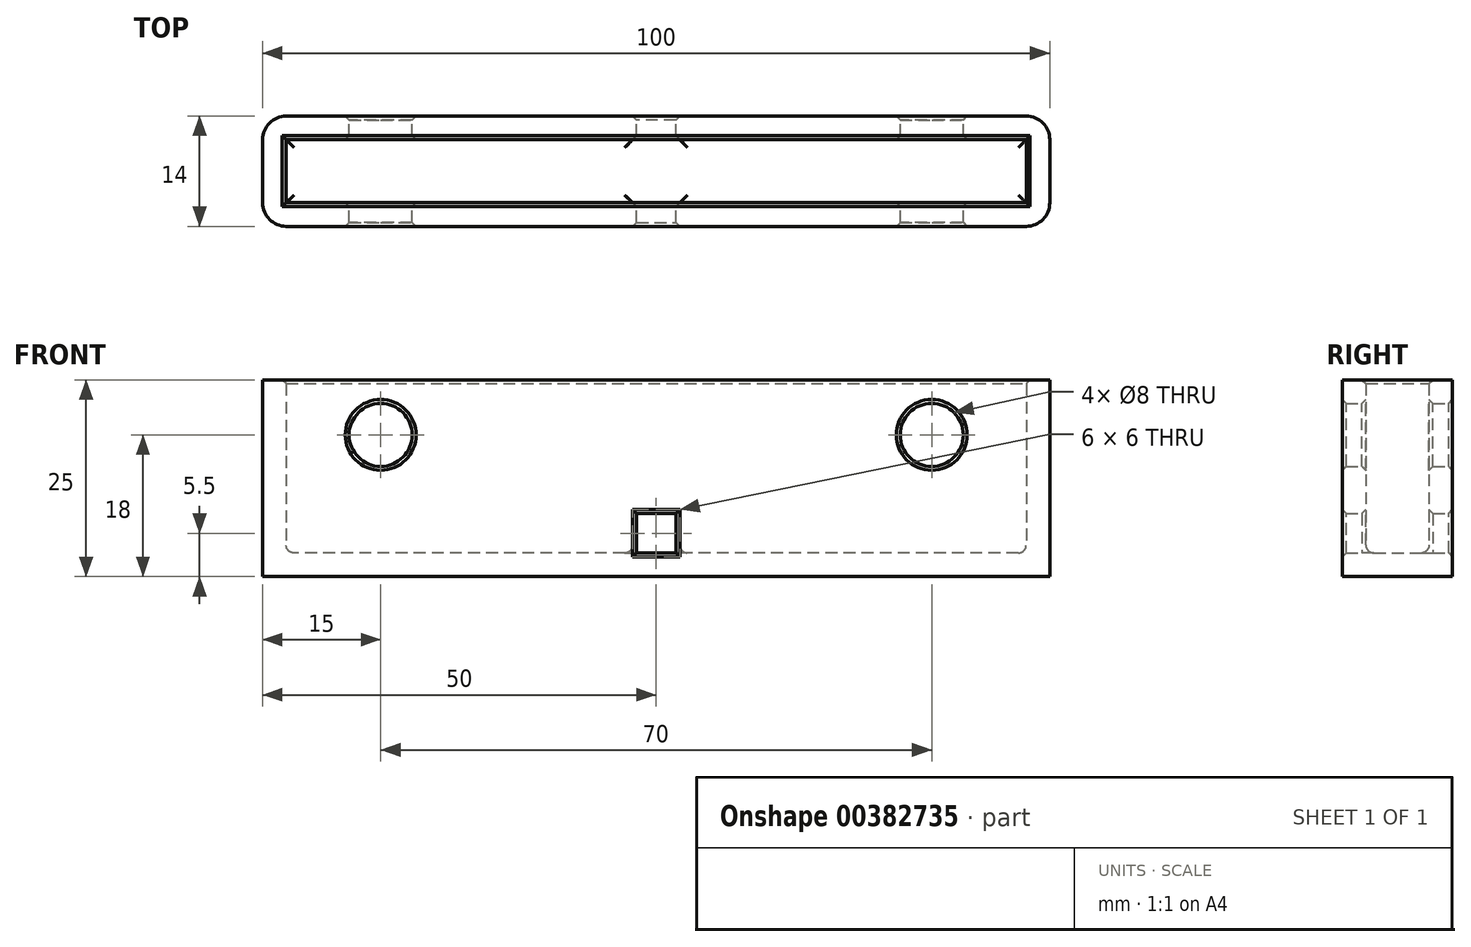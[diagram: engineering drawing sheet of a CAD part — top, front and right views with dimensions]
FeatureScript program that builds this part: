
annotation { "Feature Type Name" : "Feature", "Feature Type Description" : "" }
export const myFeature = defineFeature(function(context is Context, id is Id, definition is map)
    precondition{}
    {
        {
            var Q0;
            Q0=qCreatedBy(makeId("Top.planeOp"),FACE);
            var sketch = newSketch(context, id + "F0", { "sketchPlane" : qUnion([Q0])});
            skLineSegment(sketch, "E0.bottom", {"start": v(50, -7) * mm, "end": v(-50, -7) * mm});
            skLineSegment(sketch, "E0.top", {"start": v(50, 7) * mm, "end": v(-50, 7) * mm});
            skLineSegment(sketch, "E0.left", {"start": v(50, -7) * mm, "end": v(50, 7) * mm});
            skLineSegment(sketch, "E0.right", {"start": v(-50, -7) * mm, "end": v(-50, 7) * mm});
            skPoint(sketch, "E0.middle", {"position": v(0, 0) * mm});
            skSolve(sketch);
        }
        {
            var Q0;
            Q0=makeQuery(id+"F0.imprint","IMPRINT",FACE,{"disambiguationData":[TD([[makeQuery(id+"F0.imprint","IMPRINT",EDGE,{"derivedFrom":sQuery(id+"F0.wireOp",EDGE,"E0.bottom")}),-1.0]])]});
            extrude(context, id + "F1", {"entities" : qUnion([Q0]), "depth" : 25 * mm});
        }
        {
            var Q0;
            Q0=makeQuery(id+"F1.opExtrude","CAP_FACE",FACE,{"disambiguationData":[OSD([sQuery(id+"F0.wireOp",EDGE,"E0.bottom"),sQuery(id+"F0.wireOp",EDGE,"E0.top"),sQuery(id+"F0.wireOp",EDGE,"E0.left"),sQuery(id+"F0.wireOp",EDGE,"E0.right")])],"isStart":false});
            shell(context, id + "F2", {"entities" : qUnion([Q0]), "thickness" : 3 * mm});
        }
        {
            var Q0;
            Q0=qCreatedBy(makeId("Front.planeOp"),FACE);
            var sketch = newSketch(context, id + "F3", { "sketchPlane" : qUnion([Q0])});
            skCircle(sketch, "E1", {"center": v(-35, 18) * mm, "radius": 4 * mm});
            skCircle(sketch, "E2", {"center": v(35, 18) * mm, "radius": 4 * mm});
            skLineSegment(sketch, "E3.bottom", {"start": v(2.5, 8) * mm, "end": v(-2.5, 8) * mm});
            skLineSegment(sketch, "E3.top", {"start": v(2.5, 3) * mm, "end": v(-2.5, 3) * mm});
            skLineSegment(sketch, "E3.left", {"start": v(2.5, 8) * mm, "end": v(2.5, 3) * mm});
            skLineSegment(sketch, "E3.right", {"start": v(-2.5, 8) * mm, "end": v(-2.5, 3) * mm});
            skPoint(sketch, "E3.middle", {"position": v(0, 5.5) * mm});
            skSolve(sketch);
        }
        {
            var Q0;
            Q0 = qSketchRegion(id + "F3", true);
            extrude(context, id + "F4", {"entities" : qUnion([Q0]), "operationType" : NewBodyOperationType.REMOVE, "endBound" : BoundingType.THROUGH_ALL, "depth" : 25 * mm, "hasSecondDirection" : true, "secondDirectionBound" : BoundingType.THROUGH_ALL, "secondDirectionOppositeDirection" : true, "secondDirectionDepth" : 25 * mm});
        }
        {
            var Q0;
            Q0=makeQuery(id+"F1.opExtrude","SWEPT_EDGE",EDGE,{"disambiguationData":[OSD([sQuery(id+"F0.wireOp",EDGE,"E0.bottom"),sQuery(id+"F0.wireOp",EDGE,"E0.right")])]});
            var Q1;
            Q1=makeQuery(id+"F1.opExtrude","SWEPT_EDGE",EDGE,{"disambiguationData":[OSD([sQuery(id+"F0.wireOp",EDGE,"E0.bottom"),sQuery(id+"F0.wireOp",EDGE,"E0.left")])]});
            var Q2;
            Q2=makeQuery(id+"F1.opExtrude","SWEPT_EDGE",EDGE,{"disambiguationData":[OSD([sQuery(id+"F0.wireOp",EDGE,"E0.top"),sQuery(id+"F0.wireOp",EDGE,"E0.left")])]});
            var Q3;
            Q3=makeQuery(id+"F1.opExtrude","SWEPT_EDGE",EDGE,{"disambiguationData":[OSD([sQuery(id+"F0.wireOp",EDGE,"E0.top"),sQuery(id+"F0.wireOp",EDGE,"E0.right")])]});
            fillet(context, id + "F5", {"entities" : qUnion([Q0, Q1, Q2, Q3]), "radius" : 3 * mm, "tangentPropagation" : true, "allowEdgeOverflow" : false});
        }
        {
            var Q0;
            {var subQ0=sQuery(id+"F0.wireOp",EDGE,"E0.top");Q0=makeQuery(id+"F2.opShell","OFFSET_EDGE",EDGE,{"disambiguationData":[OSD([subQ0]),TDD([makeQuery(id+"F1.opExtrude","CAP_EDGE",EDGE,{"disambiguationData":[OSD([subQ0])],"isStart":false})])]});}
            var Q1;
            {var subQ0=sQuery(id+"F0.wireOp",EDGE,"E0.bottom");Q1=makeQuery(id+"F2.opShell","OFFSET_EDGE",EDGE,{"disambiguationData":[OSD([subQ0]),TDD([makeQuery(id+"F1.opExtrude","CAP_EDGE",EDGE,{"disambiguationData":[OSD([subQ0])],"isStart":false})])]});}
            var Q2;
            {var subQ0=sQuery(id+"F0.wireOp",EDGE,"E0.right");Q2=makeQuery(id+"F2.opShell","OFFSET_EDGE",EDGE,{"disambiguationData":[OSD([subQ0]),TDD([makeQuery(id+"F1.opExtrude","CAP_EDGE",EDGE,{"disambiguationData":[OSD([subQ0])],"isStart":false})])]});}
            var Q3;
            {var subQ0=sQuery(id+"F0.wireOp",EDGE,"E0.left");Q3=makeQuery(id+"F2.opShell","OFFSET_EDGE",EDGE,{"disambiguationData":[OSD([subQ0]),TDD([makeQuery(id+"F1.opExtrude","CAP_EDGE",EDGE,{"disambiguationData":[OSD([subQ0])],"isStart":false})])]});}
            var Q4;
            {var subQ0=sQuery(id+"F0.wireOp",EDGE,"E0.top");Q4=makeQuery(id+"F4.boolean.opBoolean","COPY",FACE,{"disambiguationData":[TD([makeQuery(id+"F1.opExtrude","SWEPT_FACE",FACE,{"disambiguationData":[OSD([subQ0])]})])],"derivedFrom":makeQuery(id+"F4.opExtrude","SWEPT_FACE",FACE,{"disambiguationData":[OSD([sQuery(id+"F3.wireOp",EDGE,"E2")])]})});}
            var Q5;
            {var subQ0=sQuery(id+"F0.wireOp",EDGE,"E0.bottom");Q5=makeQuery(id+"F4.boolean.opBoolean","COPY",FACE,{"disambiguationData":[TD([makeQuery(id+"F1.opExtrude","SWEPT_FACE",FACE,{"disambiguationData":[OSD([subQ0])]})])],"derivedFrom":makeQuery(id+"F4.opExtrude","SWEPT_FACE",FACE,{"disambiguationData":[OSD([sQuery(id+"F3.wireOp",EDGE,"E2")])]})});}
            var Q6;
            {var subQ0=sQuery(id+"F0.wireOp",EDGE,"E0.top");Q6=makeQuery(id+"F4.boolean.opBoolean","COPY",FACE,{"disambiguationData":[TD([makeQuery(id+"F1.opExtrude","SWEPT_FACE",FACE,{"disambiguationData":[OSD([subQ0])]})])],"derivedFrom":makeQuery(id+"F4.opExtrude","SWEPT_FACE",FACE,{"disambiguationData":[OSD([sQuery(id+"F3.wireOp",EDGE,"E1")])]})});}
            var Q7;
            {var subQ0=sQuery(id+"F0.wireOp",EDGE,"E0.bottom");Q7=makeQuery(id+"F4.boolean.opBoolean","COPY",FACE,{"disambiguationData":[TD([makeQuery(id+"F1.opExtrude","SWEPT_FACE",FACE,{"disambiguationData":[OSD([subQ0])]})])],"derivedFrom":makeQuery(id+"F4.opExtrude","SWEPT_FACE",FACE,{"disambiguationData":[OSD([sQuery(id+"F3.wireOp",EDGE,"E1")])]})});}
            var Q8;
            Q8=makeQuery(id+"F4.boolean.opBoolean","INTERSECT",EDGE,{"derivedFrom":[makeQuery(id+"F2.opShell","OFFSET_FACE",FACE,{"disambiguationData":[OSD([sQuery(id+"F0.wireOp",EDGE,"E0.bottom")])]}),makeQuery(id+"F4.opExtrude","SWEPT_FACE",FACE,{"disambiguationData":[OSD([sQuery(id+"F3.wireOp",EDGE,"E3.right")])]})]});
            var Q9;
            Q9=makeQuery(id+"F4.boolean.opBoolean","INTERSECT",EDGE,{"derivedFrom":[makeQuery(id+"F2.opShell","OFFSET_FACE",FACE,{"disambiguationData":[OSD([sQuery(id+"F0.wireOp",EDGE,"E0.bottom")])]}),makeQuery(id+"F4.opExtrude","SWEPT_FACE",FACE,{"disambiguationData":[OSD([sQuery(id+"F3.wireOp",EDGE,"E3.bottom")])]})]});
            var Q10;
            Q10=makeQuery(id+"F4.boolean.opBoolean","INTERSECT",EDGE,{"derivedFrom":[makeQuery(id+"F2.opShell","OFFSET_FACE",FACE,{"disambiguationData":[OSD([sQuery(id+"F0.wireOp",EDGE,"E0.bottom")])]}),makeQuery(id+"F4.opExtrude","SWEPT_FACE",FACE,{"disambiguationData":[OSD([sQuery(id+"F3.wireOp",EDGE,"E3.left")])]})]});
            var Q11;
            Q11=makeQuery(id+"F4.boolean.opBoolean","INTERSECT",EDGE,{"derivedFrom":[makeQuery(id+"F2.opShell","OFFSET_FACE",FACE,{"disambiguationData":[OSD([sQuery(id+"F0.wireOp",EDGE,"E0.top")])]}),makeQuery(id+"F4.opExtrude","SWEPT_FACE",FACE,{"disambiguationData":[OSD([sQuery(id+"F3.wireOp",EDGE,"E3.right")])]})]});
            var Q12;
            Q12=makeQuery(id+"F4.boolean.opBoolean","INTERSECT",EDGE,{"derivedFrom":[makeQuery(id+"F2.opShell","OFFSET_FACE",FACE,{"disambiguationData":[OSD([sQuery(id+"F0.wireOp",EDGE,"E0.top")])]}),makeQuery(id+"F4.opExtrude","SWEPT_FACE",FACE,{"disambiguationData":[OSD([sQuery(id+"F3.wireOp",EDGE,"E3.bottom")])]})]});
            var Q13;
            Q13=makeQuery(id+"F4.boolean.opBoolean","INTERSECT",EDGE,{"derivedFrom":[makeQuery(id+"F2.opShell","OFFSET_FACE",FACE,{"disambiguationData":[OSD([sQuery(id+"F0.wireOp",EDGE,"E0.top")])]}),makeQuery(id+"F4.opExtrude","SWEPT_FACE",FACE,{"disambiguationData":[OSD([sQuery(id+"F3.wireOp",EDGE,"E3.left")])]})]});
            var Q14;
            Q14=makeQuery(id+"F4.boolean.opBoolean","INTERSECT",EDGE,{"derivedFrom":[makeQuery(id+"F1.opExtrude","SWEPT_FACE",FACE,{"disambiguationData":[OSD([sQuery(id+"F0.wireOp",EDGE,"E0.bottom")])]}),makeQuery(id+"F4.opExtrude","SWEPT_FACE",FACE,{"disambiguationData":[OSD([sQuery(id+"F3.wireOp",EDGE,"E3.right")])]})]});
            var Q15;
            Q15=makeQuery(id+"F4.boolean.opBoolean","INTERSECT",EDGE,{"derivedFrom":[makeQuery(id+"F1.opExtrude","SWEPT_FACE",FACE,{"disambiguationData":[OSD([sQuery(id+"F0.wireOp",EDGE,"E0.bottom")])]}),makeQuery(id+"F4.opExtrude","SWEPT_FACE",FACE,{"disambiguationData":[OSD([sQuery(id+"F3.wireOp",EDGE,"E3.bottom")])]})]});
            var Q16;
            Q16=makeQuery(id+"F4.boolean.opBoolean","INTERSECT",EDGE,{"derivedFrom":[makeQuery(id+"F1.opExtrude","SWEPT_FACE",FACE,{"disambiguationData":[OSD([sQuery(id+"F0.wireOp",EDGE,"E0.bottom")])]}),makeQuery(id+"F4.opExtrude","SWEPT_FACE",FACE,{"disambiguationData":[OSD([sQuery(id+"F3.wireOp",EDGE,"E3.left")])]})]});
            var Q17;
            Q17=makeQuery(id+"F4.boolean.opBoolean","INTERSECT",EDGE,{"derivedFrom":[makeQuery(id+"F1.opExtrude","SWEPT_FACE",FACE,{"disambiguationData":[OSD([sQuery(id+"F0.wireOp",EDGE,"E0.bottom")])]}),makeQuery(id+"F4.opExtrude","SWEPT_FACE",FACE,{"disambiguationData":[OSD([sQuery(id+"F3.wireOp",EDGE,"E3.top")])]})]});
            var Q18;
            Q18=makeQuery(id+"F4.boolean.opBoolean","INTERSECT",EDGE,{"derivedFrom":[makeQuery(id+"F1.opExtrude","SWEPT_FACE",FACE,{"disambiguationData":[OSD([sQuery(id+"F0.wireOp",EDGE,"E0.top")])]}),makeQuery(id+"F4.opExtrude","SWEPT_FACE",FACE,{"disambiguationData":[OSD([sQuery(id+"F3.wireOp",EDGE,"E3.left")])]})]});
            var Q19;
            Q19=makeQuery(id+"F4.boolean.opBoolean","INTERSECT",EDGE,{"derivedFrom":[makeQuery(id+"F1.opExtrude","SWEPT_FACE",FACE,{"disambiguationData":[OSD([sQuery(id+"F0.wireOp",EDGE,"E0.top")])]}),makeQuery(id+"F4.opExtrude","SWEPT_FACE",FACE,{"disambiguationData":[OSD([sQuery(id+"F3.wireOp",EDGE,"E3.bottom")])]})]});
            var Q20;
            Q20=makeQuery(id+"F4.boolean.opBoolean","INTERSECT",EDGE,{"derivedFrom":[makeQuery(id+"F1.opExtrude","SWEPT_FACE",FACE,{"disambiguationData":[OSD([sQuery(id+"F0.wireOp",EDGE,"E0.top")])]}),makeQuery(id+"F4.opExtrude","SWEPT_FACE",FACE,{"disambiguationData":[OSD([sQuery(id+"F3.wireOp",EDGE,"E3.right")])]})]});
            var Q21;
            Q21=makeQuery(id+"F4.boolean.opBoolean","INTERSECT",EDGE,{"derivedFrom":[makeQuery(id+"F1.opExtrude","SWEPT_FACE",FACE,{"disambiguationData":[OSD([sQuery(id+"F0.wireOp",EDGE,"E0.top")])]}),makeQuery(id+"F4.opExtrude","SWEPT_FACE",FACE,{"disambiguationData":[OSD([sQuery(id+"F3.wireOp",EDGE,"E3.top")])]})]});
            chamfer(context, id + "F6", {"entities" : qUnion([Q0, Q1, Q2, Q3, Q4, Q5, Q6, Q7, Q8, Q9, Q10, Q11, Q12, Q13, Q14, Q15, Q16, Q17, Q18, Q19, Q20, Q21]), "width" : 0.5 * mm, "tangentPropagation" : true});
        }
        {
            var Q0;
            {var subQ0=sQuery(id+"F0.wireOp",EDGE,"E0.right");var subQ1=sQuery(id+"F0.wireOp",EDGE,"E0.top");Q0=makeQuery(id+"F4.boolean.opBoolean","SPLIT",EDGE,{"disambiguationData":[TD([makeQuery(id+"F2.opShell","OFFSET_FACE",FACE,{"disambiguationData":[OSD([subQ0])]})])],"derivedFrom":makeQuery(id+"F2.opShell","OFFSET_EDGE",EDGE,{"disambiguationData":[OSD([subQ1]),TDD([makeQuery(id+"F1.opExtrude","CAP_EDGE",EDGE,{"disambiguationData":[OSD([subQ1])],"isStart":true})])]})});}
            var Q1;
            {var subQ0=sQuery(id+"F0.wireOp",EDGE,"E0.right");Q1=makeQuery(id+"F2.opShell","OFFSET_EDGE",EDGE,{"disambiguationData":[OSD([subQ0]),TDD([makeQuery(id+"F1.opExtrude","CAP_EDGE",EDGE,{"disambiguationData":[OSD([subQ0])],"isStart":true})])]});}
            var Q2;
            {var subQ0=sQuery(id+"F0.wireOp",EDGE,"E0.right");var subQ1=sQuery(id+"F0.wireOp",EDGE,"E0.bottom");Q2=makeQuery(id+"F4.boolean.opBoolean","SPLIT",EDGE,{"disambiguationData":[TD([makeQuery(id+"F2.opShell","OFFSET_FACE",FACE,{"disambiguationData":[OSD([subQ0])]})])],"derivedFrom":makeQuery(id+"F2.opShell","OFFSET_EDGE",EDGE,{"disambiguationData":[OSD([subQ1]),TDD([makeQuery(id+"F1.opExtrude","CAP_EDGE",EDGE,{"disambiguationData":[OSD([subQ1])],"isStart":true})])]})});}
            var Q3;
            {var subQ0=sQuery(id+"F0.wireOp",EDGE,"E0.left");var subQ1=sQuery(id+"F0.wireOp",EDGE,"E0.bottom");Q3=makeQuery(id+"F4.boolean.opBoolean","SPLIT",EDGE,{"disambiguationData":[TD([makeQuery(id+"F2.opShell","OFFSET_FACE",FACE,{"disambiguationData":[OSD([subQ0])]})])],"derivedFrom":makeQuery(id+"F2.opShell","OFFSET_EDGE",EDGE,{"disambiguationData":[OSD([subQ1]),TDD([makeQuery(id+"F1.opExtrude","CAP_EDGE",EDGE,{"disambiguationData":[OSD([subQ1])],"isStart":true})])]})});}
            var Q4;
            {var subQ0=sQuery(id+"F0.wireOp",EDGE,"E0.left");Q4=makeQuery(id+"F2.opShell","OFFSET_EDGE",EDGE,{"disambiguationData":[OSD([subQ0]),TDD([makeQuery(id+"F1.opExtrude","CAP_EDGE",EDGE,{"disambiguationData":[OSD([subQ0])],"isStart":true})])]});}
            var Q5;
            {var subQ0=sQuery(id+"F0.wireOp",EDGE,"E0.left");var subQ1=sQuery(id+"F0.wireOp",EDGE,"E0.top");Q5=makeQuery(id+"F4.boolean.opBoolean","SPLIT",EDGE,{"disambiguationData":[TD([makeQuery(id+"F2.opShell","OFFSET_FACE",FACE,{"disambiguationData":[OSD([subQ0])]})])],"derivedFrom":makeQuery(id+"F2.opShell","OFFSET_EDGE",EDGE,{"disambiguationData":[OSD([subQ1]),TDD([makeQuery(id+"F1.opExtrude","CAP_EDGE",EDGE,{"disambiguationData":[OSD([subQ1])],"isStart":true})])]})});}
            fillet(context, id + "F7", {"entities" : qUnion([Q0, Q1, Q2, Q3, Q4, Q5]), "radius" : 1 * mm, "tangentPropagation" : true, "allowEdgeOverflow" : false});
        }
    });
